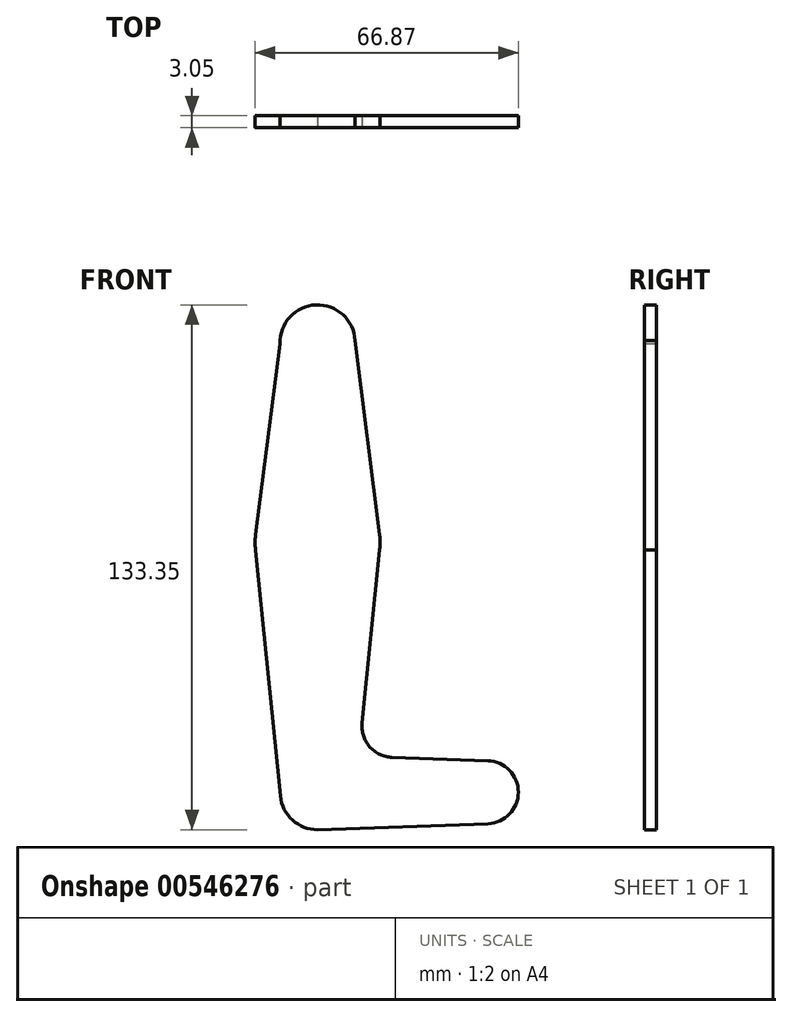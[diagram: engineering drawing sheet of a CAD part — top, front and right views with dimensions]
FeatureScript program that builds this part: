
annotation { "Feature Type Name" : "Feature", "Feature Type Description" : "" }
export const myFeature = defineFeature(function(context is Context, id is Id, definition is map)
    precondition{}
    {
        {
            var Q0;
            Q0=qCreatedBy(makeId("Front.planeOp"),FACE);
            var sketch = newSketch(context, id + "F0", { "sketchPlane" : qUnion([Q0])});
            skCircle(sketch, "E0", {"center": v(0, 85.19) * mm, "radius": 9.53 * mm});
            skCircle(sketch, "E1", {"center": v(0, -29.11) * mm, "radius": 9.53 * mm});
            skCircle(sketch, "E2", {"center": v(43, -29.11) * mm, "radius": 7.99 * mm});
            skCircle(sketch, "E3", {"center": v(0, 34.39) * mm, "radius": 15.88 * mm});
            skLineSegment(sketch, "E4", {"start": v(9.52, 85.62) * mm, "end": v(15.75, 36.38) * mm});
            skLineSegment(sketch, "E5", {"start": v(-9.52, 84.83) * mm, "end": v(-15.75, 36.41) * mm});
            skLineSegment(sketch, "E6", {"start": v(-15.75, 32.36) * mm, "end": v(-9.48, -30.07) * mm});
            skLineSegment(sketch, "E7", {"start": v(11.3, -11.52) * mm, "end": v(15.75, 32.4) * mm});
            skLineSegment(sketch, "E8", {"start": v(0, -38.64) * mm, "end": v(43.3, -37.1) * mm});
            skLineSegment(sketch, "E9", {"start": v(18.93, -20.26) * mm, "end": v(43.3, -21.13) * mm});
            skCircle(sketch, "E10", {"center": v(0, 85.19) * mm, "radius": 3.44 * mm});
            skCircle(sketch, "E11", {"center": v(0, 34.39) * mm, "radius": 3.18 * mm});
            skCircle(sketch, "E12", {"center": v(43, -29.11) * mm, "radius": 3.18 * mm});
            skCircle(sketch, "E13", {"center": v(0, -29.11) * mm, "radius": 3.18 * mm});
            skCircle(sketch, "E14", {"center": v(-4.96, 70.91) * mm, "radius": 3.18 * mm});
            skPoint(sketch, "E15.newPointA", {"position": v(9.53, -29.11) * mm});
            skPoint(sketch, "E15.newPointB", {"position": v(0, -19.59) * mm});
            skArc(sketch, "E15.filletArc", {"start": v(11.3, -11.52) * mm, "mid": v(13.22, -17.54) * mm, "end": v(18.93, -20.26) * mm});
            skSolve(sketch);
        }
        {
            var Q0;
            Q0=makeQuery(id+"F0.imprint","IMPRINT",FACE,{"disambiguationData":[TD([[makeQuery(id+"F0.imprint","IMPRINT",EDGE,{"derivedFrom":sQuery(id+"F0.wireOp",EDGE,"E10")}),-1.0]])]});
            var Q1;
            Q1=makeQuery(id+"F0.imprint","IMPRINT",FACE,{"disambiguationData":[TD([[makeQuery(id+"F0.imprint","IMPRINT",EDGE,{"derivedFrom":sQuery(id+"F0.wireOp",EDGE,"E12")}),-1.0]])]});
            var Q2;
            {var subQ1=sQuery(id+"F0.wireOp",EDGE,"E4");Q2=makeQuery(id+"F0.imprint","IMPRINT",FACE,{"disambiguationData":[TD([[makeQuery(id+"F0.imprint","IMPRINT",EDGE,{"derivedFrom":subQ1}),-1.0]])]});}
            var Q3;
            Q3=makeQuery(id+"F0.imprint","IMPRINT",FACE,{"disambiguationData":[TD([[makeQuery(id+"F0.imprint","IMPRINT",EDGE,{"derivedFrom":sQuery(id+"F0.wireOp",EDGE,"E13")}),-1.0]])]});
            var Q4;
            {var subQ0=sQuery(id+"F0.wireOp",EDGE,"E6");Q4=makeQuery(id+"F0.imprint","IMPRINT",FACE,{"disambiguationData":[TD([[makeQuery(id+"F0.imprint","IMPRINT",EDGE,{"derivedFrom":subQ0}),1.0]])]});}
            var Q5;
            Q5=makeQuery(id+"F0.imprint","IMPRINT",FACE,{"disambiguationData":[TD([[makeQuery(id+"F0.imprint","IMPRINT",EDGE,{"derivedFrom":sQuery(id+"F0.wireOp",EDGE,"E11")}),-1.0]])]});
            var Q6;
            Q6=makeQuery(id+"F0.imprint","IMPRINT",FACE,{"disambiguationData":[TD([[makeQuery(id+"F0.imprint","IMPRINT",EDGE,{"derivedFrom":sQuery(id+"F0.wireOp",EDGE,"E14")}),1.0]])]});
            var Q7;
            Q7=makeQuery(id+"F0.imprint","IMPRINT",FACE,{"disambiguationData":[TD([[makeQuery(id+"F0.imprint","IMPRINT",EDGE,{"derivedFrom":sQuery(id+"F0.wireOp",EDGE,"E13")}),1.0]])]});
            var Q8;
            Q8=makeQuery(id+"F0.imprint","IMPRINT",FACE,{"disambiguationData":[TD([[makeQuery(id+"F0.imprint","IMPRINT",EDGE,{"derivedFrom":sQuery(id+"F0.wireOp",EDGE,"E12")}),1.0]])]});
            var Q9;
            {var subQ0=sQuery(id+"F0.wireOp",EDGE,"E8");var subQ1=sQuery(id+"F0.wireOp",EDGE,"E1");var subQ2=makeQuery(id+"F0.imprint","INTERSECT",VERTEX,{"disambiguationData":[OD(0.0)],"derivedFrom":[subQ1,subQ0]});Q9=makeQuery(id+"F0.imprint","IMPRINT",FACE,{"disambiguationData":[TD([[makeQuery(id+"F0.imprint","IMPRINT",EDGE,{"disambiguationData":[TD([[subQ2,-1.0]])],"derivedFrom":subQ1}),1.0]])]});}
            var Q10;
            Q10=makeQuery(id+"F0.imprint","IMPRINT",FACE,{"disambiguationData":[TD([[makeQuery(id+"F0.imprint","IMPRINT",EDGE,{"derivedFrom":sQuery(id+"F0.wireOp",EDGE,"E10")}),1.0]])]});
            var Q11;
            Q11=makeQuery(id+"F0.imprint","IMPRINT",FACE,{"disambiguationData":[TD([[makeQuery(id+"F0.imprint","IMPRINT",EDGE,{"derivedFrom":sQuery(id+"F0.wireOp",EDGE,"E11")}),1.0]])]});
            extrude(context, id + "F1", {"entities" : qUnion([Q0, Q1, Q2, Q3, Q4, Q5, Q6, Q7, Q8, Q9, Q10, Q11]), "oppositeDirection" : true, "depth" : 3.05 * mm, "offsetDistance" : 25.4 * mm});
        }
    });
